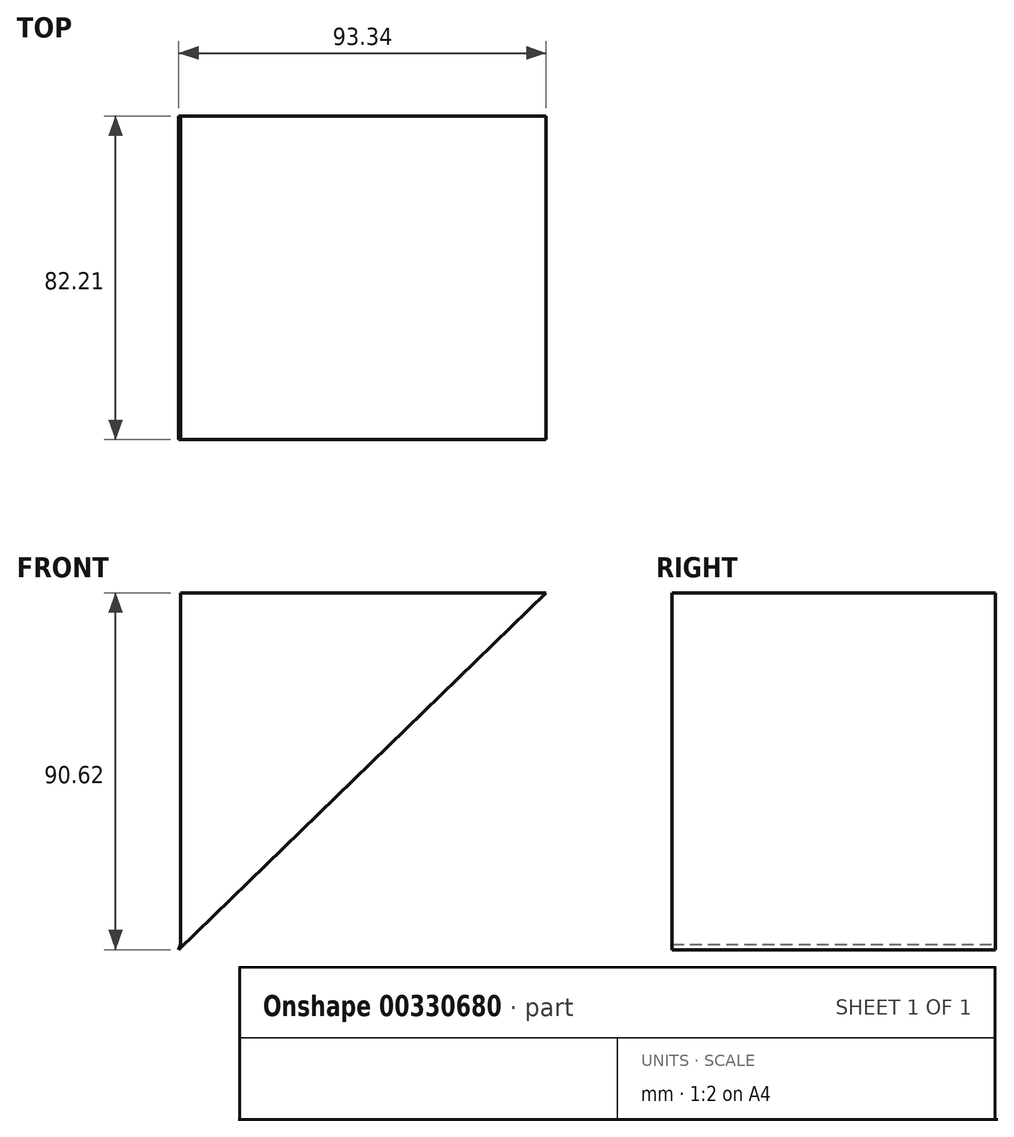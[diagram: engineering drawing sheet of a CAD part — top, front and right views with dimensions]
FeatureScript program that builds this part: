
annotation { "Feature Type Name" : "Feature", "Feature Type Description" : "" }
export const myFeature = defineFeature(function(context is Context, id is Id, definition is map)
    precondition{}
    {
        {
            var Q0;
            Q0=qCreatedBy(makeId("Front.planeOp"),FACE);
            var sketch = newSketch(context, id + "F0", { "sketchPlane" : qUnion([Q0])});
            skLineSegment(sketch, "E0", {"start": v(-46.08, 49.22) * mm, "end": v(-46.08, -40.09) * mm});
            skLineSegment(sketch, "E1", {"start": v(-46.08, -40.09) * mm, "end": v(-46.6, -41.4) * mm});
            skLineSegment(sketch, "E2", {"start": v(-46.6, -41.4) * mm, "end": v(46.75, 49.22) * mm});
            skLineSegment(sketch, "E3", {"start": v(46.75, 49.22) * mm, "end": v(-46.08, 49.22) * mm});
            skSolve(sketch);
        }
        {
            var Q0;
            Q0=makeQuery(id+"F0.imprint","IMPRINT",FACE,{"disambiguationData":[TD([[makeQuery(id+"F0.imprint","IMPRINT",EDGE,{"derivedFrom":sQuery(id+"F0.wireOp",EDGE,"E0")}),1.0]])]});
            extrude(context, id + "F1", {"entities" : qUnion([Q0]), "depth" : 82.2 * mm});
        }
    });
